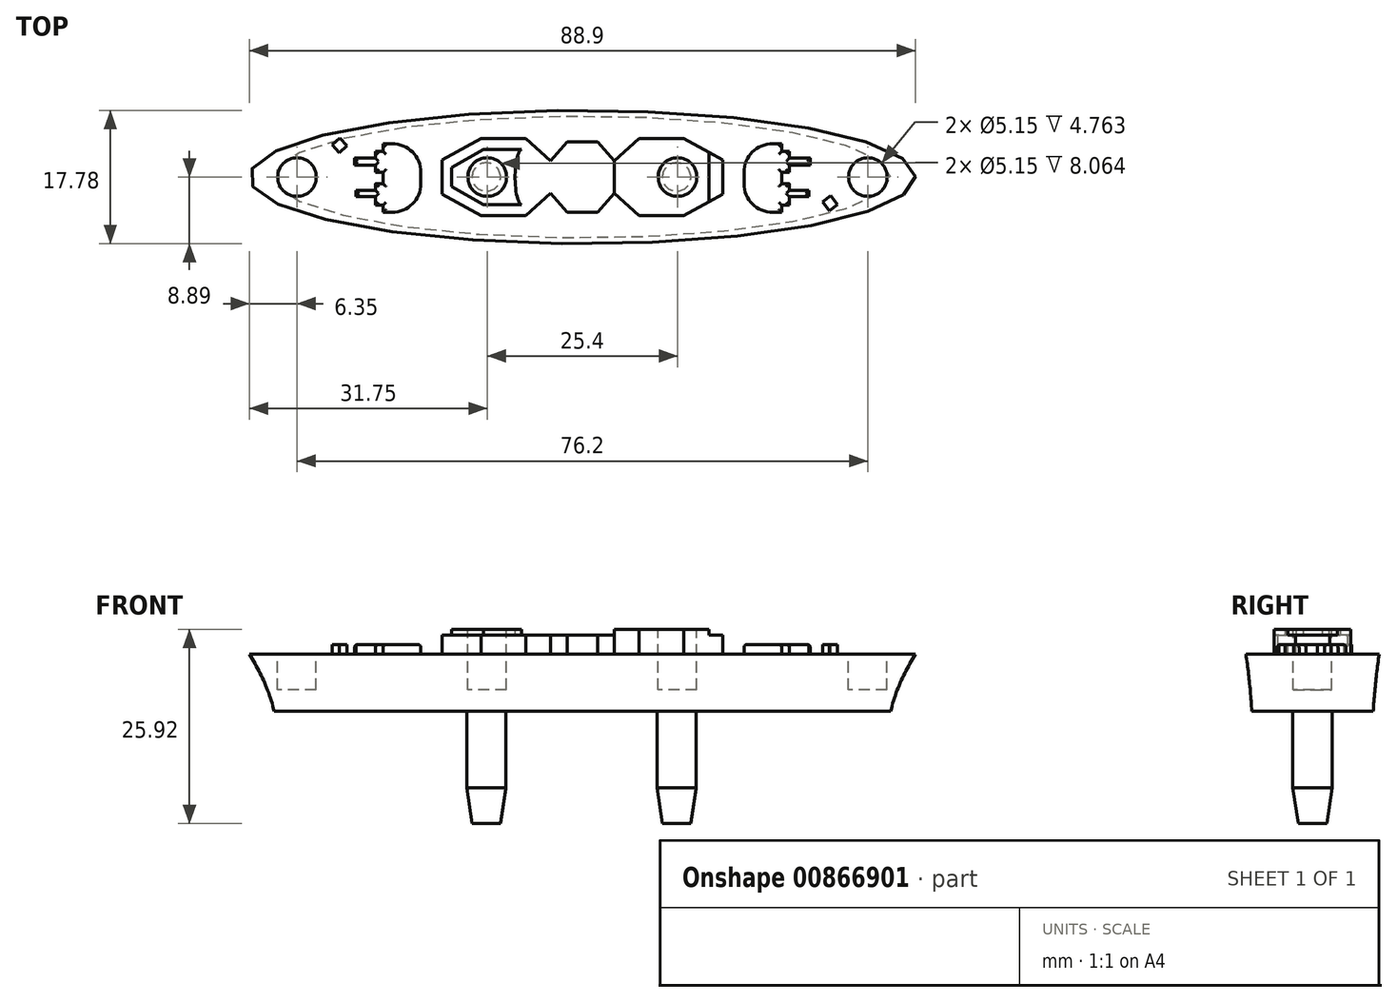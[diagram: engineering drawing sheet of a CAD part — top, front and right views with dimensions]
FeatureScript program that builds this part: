
annotation { "Feature Type Name" : "Feature", "Feature Type Description" : "" }
export const myFeature = defineFeature(function(context is Context, id is Id, definition is map)
    precondition{}
    {
        {
            var Q0;
            Q0=qCreatedBy(makeId("Top.planeOp"),FACE);
            var sketch = newSketch(context, id + "F0", { "sketchPlane" : qUnion([Q0])});
            skEllipse(sketch, "E0", {"center": v(0, 0) * mm, "majorRadius": 44.45 * mm, "minorRadius": 8.9 * mm, "majorAxis": v(1, 0)});
            skSolve(sketch);
        }
        {
            var Q0;
            Q0=qCreatedBy(makeId("Top.planeOp"),FACE);
            cPlane(context, id + "F1", {"entities" : qUnion([Q0]), "cplaneType" : CPlaneType.OFFSET, "offset" : 7.62 * mm, "oppositeDirection" : true, "width" : 152.4 * mm, "height" : 152.4 * mm});
        }
        {
            var Q0;
            Q0=qCreatedBy(id+"F1.planeOp",FACE);
            var sketch = newSketch(context, id + "F2", { "sketchPlane" : qUnion([Q0])});
            skEllipse(sketch, "E1", {"center": v(0, 0) * mm, "majorRadius": 41.16 * mm, "minorRadius": 8.1 * mm, "majorAxis": v(1, 0)});
            skSolve(sketch);
        }
        {
            var Q0;
            Q0=makeQuery(id+"F2.imprint","IMPRINT",FACE,{"disambiguationData":[TD([[makeQuery(id+"F2.imprint","IMPRINT",EDGE,{"derivedFrom":sQuery(id+"F2.wireOp",EDGE,"E1")}),1.0]])]});
            var Q1;
            Q1=makeQuery(id+"F0.imprint","IMPRINT",FACE,{"disambiguationData":[TD([[makeQuery(id+"F0.imprint","IMPRINT",EDGE,{"derivedFrom":sQuery(id+"F0.wireOp",EDGE,"E0")}),1.0]])]});
            loft(context, id + "F3", {"sheetProfilesArray" : [{ "sheetProfileEntities" : qUnion([Q0]) }, { "sheetProfileEntities" : qUnion([Q1]) }]});
        }
        {
            var Q0;
            Q0=qCreatedBy(id+"F1.planeOp",FACE);
            var sketch = newSketch(context, id + "F4", { "sketchPlane" : qUnion([Q0])});
            skLineSegment(sketch, "E2", {"start": v(-38.24, 0) * mm, "end": v(-12.84, 0) * mm, "construction": true});
            skLineSegment(sketch, "E3", {"start": v(-12.84, 0) * mm, "end": v(12.56, 0) * mm, "construction": true});
            skLineSegment(sketch, "E4", {"start": v(12.56, 0) * mm, "end": v(37.96, 0) * mm, "construction": true});
            skCircle(sketch, "E5", {"center": v(37.96, 0) * mm, "radius": 2.62 * mm});
            skCircle(sketch, "E6", {"center": v(12.56, 0) * mm, "radius": 2.62 * mm});
            skCircle(sketch, "E7", {"center": v(-12.84, 0) * mm, "radius": 2.62 * mm});
            skCircle(sketch, "E8", {"center": v(-38.24, 0) * mm, "radius": 2.62 * mm});
            skSolve(sketch);
        }
        {
            var Q0;
            Q0=makeQuery(id+"F4.imprint","IMPRINT",FACE,{"disambiguationData":[TD([[makeQuery(id+"F4.imprint","IMPRINT",EDGE,{"derivedFrom":sQuery(id+"F4.wireOp",EDGE,"E7")}),1.0]])]});
            var Q1;
            Q1=makeQuery(id+"F4.imprint","IMPRINT",FACE,{"disambiguationData":[TD([[makeQuery(id+"F4.imprint","IMPRINT",EDGE,{"derivedFrom":sQuery(id+"F4.wireOp",EDGE,"E6")}),1.0]])]});
            extrude(context, id + "F5", {"entities" : qUnion([Q0, Q1]), "operationType" : NewBodyOperationType.ADD, "oppositeDirection" : true, "depth" : 15 * mm, "offsetDistance" : 25.4 * mm});
        }
        {
            var Q0;
            Q0=makeQuery(id+"F3.opLoft","CAP_FACE",FACE,{"disambiguationData":[OSD([makeQuery(id+"F0.imprint","IMPRINT",FACE,{"disambiguationData":[TD([[makeQuery(id+"F0.imprint","IMPRINT",EDGE,{"derivedFrom":sQuery(id+"F0.wireOp",EDGE,"E0")}),1.0]])]})])],"isStart":true});
            var sketch = newSketch(context, id + "F6", { "sketchPlane" : qUnion([Q0])});
            skLineSegment(sketch, "E9", {"start": v(-38.1, 0) * mm, "end": v(-12.7, 0) * mm, "construction": true});
            skLineSegment(sketch, "E10", {"start": v(-12.7, 0) * mm, "end": v(12.7, 0) * mm, "construction": true});
            skLineSegment(sketch, "E11", {"start": v(12.7, 0) * mm, "end": v(38.1, 0) * mm, "construction": true});
            skCircle(sketch, "E12", {"center": v(38.1, 0) * mm, "radius": 2.58 * mm});
            skCircle(sketch, "E13", {"center": v(12.7, 0) * mm, "radius": 2.58 * mm});
            skCircle(sketch, "E14", {"center": v(-12.7, 0) * mm, "radius": 2.58 * mm});
            skCircle(sketch, "E15", {"center": v(-38.1, 0) * mm, "radius": 2.58 * mm});
            skSolve(sketch);
        }
        {
            var Q0;
            Q0=makeQuery(id+"F6.imprint","IMPRINT",FACE,{"disambiguationData":[TD([[makeQuery(id+"F6.imprint","IMPRINT",EDGE,{"derivedFrom":sQuery(id+"F6.wireOp",EDGE,"E15")}),1.0]])]});
            var Q1;
            Q1=makeQuery(id+"F6.imprint","IMPRINT",FACE,{"disambiguationData":[TD([[makeQuery(id+"F6.imprint","IMPRINT",EDGE,{"derivedFrom":sQuery(id+"F6.wireOp",EDGE,"E14")}),1.0]])]});
            var Q2;
            Q2=makeQuery(id+"F6.imprint","IMPRINT",FACE,{"disambiguationData":[TD([[makeQuery(id+"F6.imprint","IMPRINT",EDGE,{"derivedFrom":sQuery(id+"F6.wireOp",EDGE,"E13")}),1.0]])]});
            var Q3;
            Q3=makeQuery(id+"F6.imprint","IMPRINT",FACE,{"disambiguationData":[TD([[makeQuery(id+"F6.imprint","IMPRINT",EDGE,{"derivedFrom":sQuery(id+"F6.wireOp",EDGE,"E12")}),1.0]])]});
            extrude(context, id + "F7", {"entities" : qUnion([Q0, Q1, Q2, Q3]), "operationType" : NewBodyOperationType.REMOVE, "oppositeDirection" : true, "depth" : 4.76 * mm, "offsetDistance" : 25.4 * mm});
        }
        {
            var Q0;
            Q0=makeQuery(id+"F5.opExtrude","CAP_EDGE",EDGE,{"disambiguationData":[OSD([sQuery(id+"F4.wireOp",EDGE,"E7")])],"isStart":false});
            var Q1;
            Q1=makeQuery(id+"F5.opExtrude","CAP_EDGE",EDGE,{"disambiguationData":[OSD([sQuery(id+"F4.wireOp",EDGE,"E6")])],"isStart":false});
            chamfer(context, id + "F8", {"entities" : qUnion([Q0, Q1]), "chamferType" : ChamferType.TWO_OFFSETS, "width1" : 4.76 * mm, "oppositeDirection" : false, "width2" : 0.73 * mm, "tangentPropagation" : true});
        }
        {
            var Q0;
            Q0=makeQuery(id+"F3.opLoft","CAP_FACE",FACE,{"disambiguationData":[OSD([makeQuery(id+"F0.imprint","IMPRINT",FACE,{"disambiguationData":[TD([[makeQuery(id+"F0.imprint","IMPRINT",EDGE,{"derivedFrom":sQuery(id+"F0.wireOp",EDGE,"E0")}),1.0]])]})])],"isStart":true});
            var sketch = newSketch(context, id + "F9", { "sketchPlane" : qUnion([Q0])});
            skLineSegment(sketch, "E16", {"start": v(0, 11.72) * mm, "end": v(0, 15.23) * mm, "construction": true});
            skLineSegment(sketch, "E17", {"start": v(0, 4.68) * mm, "end": v(2.01, 4.68) * mm});
            skLineSegment(sketch, "E18", {"start": v(2.01, 4.68) * mm, "end": v(4.23, 2.18) * mm});
            skLineSegment(sketch, "E19", {"start": v(4.23, 2.18) * mm, "end": v(7.53, 5.12) * mm});
            skLineSegment(sketch, "E20", {"start": v(7.53, 5.12) * mm, "end": v(13.53, 5.12) * mm});
            skLineSegment(sketch, "E21", {"start": v(13.53, 5.12) * mm, "end": v(18.74, 2.3) * mm});
            skLineSegment(sketch, "E22", {"start": v(18.74, 2.3) * mm, "end": v(18.74, -2.3) * mm});
            skLineSegment(sketch, "E23", {"start": v(18.74, -2.3) * mm, "end": v(13.53, -5.12) * mm});
            skLineSegment(sketch, "E24", {"start": v(13.53, -5.12) * mm, "end": v(7.53, -5.12) * mm});
            skLineSegment(sketch, "E25", {"start": v(7.53, -5.12) * mm, "end": v(4.23, -2.18) * mm});
            skLineSegment(sketch, "E26", {"start": v(4.23, -2.18) * mm, "end": v(2.01, -4.68) * mm});
            skLineSegment(sketch, "E27", {"start": v(2.01, -4.68) * mm, "end": v(0, -4.68) * mm});
            skLineSegment(sketch, "E28.MirrorCS", {"start": v(-7.53, -5.12) * mm, "end": v(-4.23, -2.18) * mm});
            skLineSegment(sketch, "E29.MirrorCS", {"start": v(-4.23, -2.18) * mm, "end": v(-2.01, -4.68) * mm});
            skLineSegment(sketch, "E30.MirrorCS", {"start": v(-2.01, 4.68) * mm, "end": v(-4.23, 2.18) * mm});
            skLineSegment(sketch, "E31.MirrorCS", {"start": v(-4.23, 2.18) * mm, "end": v(-7.53, 5.12) * mm});
            skLineSegment(sketch, "E32.MirrorCS", {"start": v(-2.01, -4.68) * mm, "end": v(0, -4.68) * mm});
            skLineSegment(sketch, "E33.MirrorCS", {"start": v(0, 4.68) * mm, "end": v(-2.01, 4.68) * mm});
            skLineSegment(sketch, "E34.MirrorCS", {"start": v(-18.74, -2.3) * mm, "end": v(-13.53, -5.12) * mm});
            skLineSegment(sketch, "E35.MirrorCS", {"start": v(-13.53, -5.12) * mm, "end": v(-7.53, -5.12) * mm});
            skLineSegment(sketch, "E36.MirrorCS", {"start": v(-18.74, 2.3) * mm, "end": v(-18.74, -2.3) * mm});
            skLineSegment(sketch, "E37.MirrorCS", {"start": v(-13.53, 5.12) * mm, "end": v(-18.74, 2.3) * mm});
            skLineSegment(sketch, "E38.MirrorCS", {"start": v(-7.53, 5.12) * mm, "end": v(-13.53, 5.12) * mm});
            skLineSegment(sketch, "E39", {"start": v(12.7, 0) * mm, "end": v(-12.7, 0) * mm, "construction": true});
            skSolve(sketch);
        }
        {
            var Q0;
            Q0=makeQuery(id+"F9.imprint","IMPRINT",FACE,{"disambiguationData":[TD([[makeQuery(id+"F9.imprint","IMPRINT",EDGE,{"derivedFrom":sQuery(id+"F9.wireOp",EDGE,"E17")}),-1.0]])]});
            extrude(context, id + "F10", {"entities" : qUnion([Q0]), "operationType" : NewBodyOperationType.ADD, "depth" : 2.54 * mm, "offsetDistance" : 25.4 * mm});
        }
        {
            var Q0;
            Q0=makeQuery(id+"F10.opExtrude","CAP_FACE",FACE,{"disambiguationData":[OSD([sQuery(id+"F6.wireOp",EDGE,"E13"),sQuery(id+"F6.wireOp",EDGE,"E14"),sQuery(id+"F9.wireOp",EDGE,"E17"),sQuery(id+"F9.wireOp",EDGE,"E18"),sQuery(id+"F9.wireOp",EDGE,"E19"),sQuery(id+"F9.wireOp",EDGE,"E20"),sQuery(id+"F9.wireOp",EDGE,"E21"),sQuery(id+"F9.wireOp",EDGE,"E22"),sQuery(id+"F9.wireOp",EDGE,"E23"),sQuery(id+"F9.wireOp",EDGE,"E24"),sQuery(id+"F9.wireOp",EDGE,"E25"),sQuery(id+"F9.wireOp",EDGE,"E26"),sQuery(id+"F9.wireOp",EDGE,"E27"),sQuery(id+"F9.wireOp",EDGE,"E28.MirrorCS"),sQuery(id+"F9.wireOp",EDGE,"E29.MirrorCS"),sQuery(id+"F9.wireOp",EDGE,"E30.MirrorCS"),sQuery(id+"F9.wireOp",EDGE,"E31.MirrorCS"),sQuery(id+"F9.wireOp",EDGE,"E32.MirrorCS"),sQuery(id+"F9.wireOp",EDGE,"E33.MirrorCS"),sQuery(id+"F9.wireOp",EDGE,"E34.MirrorCS"),sQuery(id+"F9.wireOp",EDGE,"E35.MirrorCS"),sQuery(id+"F9.wireOp",EDGE,"E36.MirrorCS"),sQuery(id+"F9.wireOp",EDGE,"E37.MirrorCS"),sQuery(id+"F9.wireOp",EDGE,"E38.MirrorCS")])],"isStart":false});
            var sketch = newSketch(context, id + "F11", { "sketchPlane" : qUnion([Q0])});
            skLineSegment(sketch, "E40", {"start": v(-8.16, 3.7) * mm, "end": v(-13.2, 3.7) * mm});
            skLineSegment(sketch, "E41", {"start": v(-13.2, -3.7) * mm, "end": v(-8.16, -3.7) * mm});
            skPoint(sketch, "E42", {"position": v(-4.23, 1.21) * mm});
            skPoint(sketch, "E43", {"position": v(0, 3.64) * mm});
            skPoint(sketch, "E44", {"position": v(2.47, 0) * mm});
            skPoint(sketch, "E45", {"position": v(0, -3.64) * mm});
            skPoint(sketch, "E46", {"position": v(-4.23, -1.21) * mm});
            skFitSpline(sketch, "E47", {"points": [v(-8.16, 3.7) * mm, v(-4.23, 1.21) * mm, v(0, 3.64) * mm, v(2.47, 0) * mm, v(0, -3.64) * mm, v(-4.23, -1.21) * mm, v(-8.16, -3.7) * mm, v(-8.16, 3.7) * mm]});
            skLineSegment(sketch, "E48", {"start": v(7.53, 5.12) * mm, "end": v(4.23, 2.18) * mm});
            skLineSegment(sketch, "E49", {"start": v(4.23, -2.18) * mm, "end": v(7.53, -5.12) * mm});
            skLineSegment(sketch, "E50", {"start": v(7.53, -5.12) * mm, "end": v(13.53, -5.12) * mm});
            skLineSegment(sketch, "E51", {"start": v(13.53, 5.12) * mm, "end": v(7.53, 5.12) * mm});
            skLineSegment(sketch, "E52", {"start": v(-12.7, 0) * mm, "end": v(12.7, 0) * mm, "construction": true});
            skPoint(sketch, "E53", {"position": v(-17.44, 1.26) * mm});
            skPoint(sketch, "E54", {"position": v(-17.44, -1.26) * mm});
            skLineSegment(sketch, "E55", {"start": v(-13.2, 3.7) * mm, "end": v(-17.44, 1.26) * mm});
            skLineSegment(sketch, "E56", {"start": v(-17.44, 1.26) * mm, "end": v(-17.44, -1.26) * mm});
            skLineSegment(sketch, "E57", {"start": v(-17.44, -1.26) * mm, "end": v(-13.2, -3.7) * mm});
            skPoint(sketch, "E58", {"position": v(16.9, 3.29) * mm});
            skPoint(sketch, "E59", {"position": v(16.9, -3.29) * mm});
            skLineSegment(sketch, "E60", {"start": v(13.53, 5.12) * mm, "end": v(16.9, 3.29) * mm});
            skLineSegment(sketch, "E61", {"start": v(16.9, 3.29) * mm, "end": v(16.9, -3.29) * mm});
            skLineSegment(sketch, "E62", {"start": v(16.9, -3.29) * mm, "end": v(13.53, -5.12) * mm});
            skLineSegment(sketch, "E63", {"start": v(4.23, 2.18) * mm, "end": v(4.23, -2.18) * mm});
            skSolve(sketch);
        }
        {
            var Q0;
            Q0=makeQuery(id+"F11.imprint","IMPRINT",FACE,{"disambiguationData":[TD([[makeQuery(id+"F11.imprint","IMPRINT",EDGE,{"derivedFrom":sQuery(id+"F11.wireOp",EDGE,"E40")}),1.0]])]});
            var Q1;
            Q1=makeQuery(id+"F11.imprint","IMPRINT",FACE,{"disambiguationData":[TD([[makeQuery(id+"F11.imprint","IMPRINT",EDGE,{"derivedFrom":sQuery(id+"F11.wireOp",EDGE,"E48")}),-1.0]])]});
            extrude(context, id + "F12", {"entities" : qUnion([Q0, Q1]), "operationType" : NewBodyOperationType.ADD, "depth" : 0.76 * mm, "offsetDistance" : 25.4 * mm});
        }
        {
            var Q0;
            Q0=makeQuery(id+"F3.opLoft","CAP_FACE",FACE,{"disambiguationData":[OSD([makeQuery(id+"F0.imprint","IMPRINT",FACE,{"disambiguationData":[TD([[makeQuery(id+"F0.imprint","IMPRINT",EDGE,{"derivedFrom":sQuery(id+"F0.wireOp",EDGE,"E0")}),1.0]])]})])],"isStart":true});
            var sketch = newSketch(context, id + "F13", { "sketchPlane" : qUnion([Q0])});
            skLineSegment(sketch, "E64", {"start": v(0, -10.91) * mm, "end": v(0, -13.7) * mm, "construction": true});
            skLineSegment(sketch, "E65.bottom", {"start": v(25.38, 4.45) * mm, "end": v(26.6, 4.45) * mm});
            skLineSegment(sketch, "E65.top", {"start": v(25.38, -4.7) * mm, "end": v(26.6, -4.7) * mm});
            skLineSegment(sketch, "E65.left", {"start": v(21.57, 0.64) * mm, "end": v(21.57, -0.9) * mm});
            skLineSegment(sketch, "E65.right", {"start": v(26.6, 4.45) * mm, "end": v(26.6, 3.41) * mm});
            skPoint(sketch, "E66.visualSharp", {"position": v(21.57, 4.45) * mm});
            skArc(sketch, "E66.filletArc", {"start": v(25.38, 4.45) * mm, "mid": v(22.68, 3.33) * mm, "end": v(21.57, 0.64) * mm});
            skPoint(sketch, "E67.visualSharp", {"position": v(21.57, -4.7) * mm});
            skArc(sketch, "E67.filletArc", {"start": v(21.57, -0.9) * mm, "mid": v(22.68, -3.6) * mm, "end": v(25.38, -4.7) * mm});
            skLineSegment(sketch, "E68.bottom", {"start": v(26.6, 3.41) * mm, "end": v(27.6, 3.41) * mm});
            skLineSegment(sketch, "E68.top", {"start": v(26.6, 0.62) * mm, "end": v(27.6, 0.62) * mm});
            skLineSegment(sketch, "E68.right", {"start": v(27.6, 3.41) * mm, "end": v(27.6, 2.5) * mm});
            skLineSegment(sketch, "E69.bottom", {"start": v(26.6, -0.89) * mm, "end": v(27.6, -0.89) * mm});
            skLineSegment(sketch, "E69.top", {"start": v(26.6, -3.75) * mm, "end": v(27.6, -3.75) * mm});
            skLineSegment(sketch, "E69.right", {"start": v(27.6, -0.89) * mm, "end": v(27.6, -1.8) * mm});
            skLineSegment(sketch, "E70.bottom", {"start": v(27.6, 2.5) * mm, "end": v(30.4, 2.5) * mm});
            skLineSegment(sketch, "E70.top", {"start": v(27.6, 1.6) * mm, "end": v(30.4, 1.6) * mm});
            skLineSegment(sketch, "E70.right", {"start": v(30.4, 2.5) * mm, "end": v(30.4, 1.6) * mm});
            skLineSegment(sketch, "E71.bottom", {"start": v(27.6, -1.8) * mm, "end": v(30.25, -1.8) * mm});
            skLineSegment(sketch, "E71.top", {"start": v(27.6, -2.62) * mm, "end": v(30.25, -2.62) * mm});
            skLineSegment(sketch, "E71.right", {"start": v(30.25, -1.8) * mm, "end": v(30.25, -2.62) * mm});
            skLineSegment(sketch, "E72.trimOffspring", {"start": v(27.6, 1.6) * mm, "end": v(27.6, 0.62) * mm});
            skLineSegment(sketch, "E73.trimOffspring", {"start": v(27.6, -2.62) * mm, "end": v(27.6, -3.75) * mm});
            skLineSegment(sketch, "E74.trimOffspring", {"start": v(26.6, -3.75) * mm, "end": v(26.6, -4.7) * mm});
            skLineSegment(sketch, "E75.trimOffspring", {"start": v(26.6, 0.62) * mm, "end": v(26.6, -0.89) * mm});
            skLineSegment(sketch, "E76.MirrorCS", {"start": v(-27.6, -0.89) * mm, "end": v(-27.6, -1.8) * mm});
            skLineSegment(sketch, "E77.MirrorCS", {"start": v(-26.6, -0.89) * mm, "end": v(-27.6, -0.89) * mm});
            skLineSegment(sketch, "E78.MirrorCS", {"start": v(-26.6, 0.62) * mm, "end": v(-27.6, 0.62) * mm});
            skLineSegment(sketch, "E79.MirrorCS", {"start": v(-27.6, 1.6) * mm, "end": v(-27.6, 0.62) * mm});
            skLineSegment(sketch, "E80.MirrorCS", {"start": v(-26.6, 0.62) * mm, "end": v(-26.6, -0.89) * mm});
            skLineSegment(sketch, "E81.MirrorCS", {"start": v(-27.6, -2.62) * mm, "end": v(-27.6, -3.75) * mm});
            skLineSegment(sketch, "E82.MirrorCS", {"start": v(-30.25, -1.8) * mm, "end": v(-30.25, -2.62) * mm});
            skLineSegment(sketch, "E83.MirrorCS", {"start": v(-26.6, -3.75) * mm, "end": v(-26.6, -4.7) * mm});
            skLineSegment(sketch, "E84.MirrorCS", {"start": v(-26.6, 3.41) * mm, "end": v(-27.6, 3.41) * mm});
            skLineSegment(sketch, "E85.MirrorCS", {"start": v(-21.57, 0.64) * mm, "end": v(-21.57, -0.9) * mm});
            skLineSegment(sketch, "E86.MirrorCS", {"start": v(-25.38, 4.45) * mm, "end": v(-26.6, 4.45) * mm});
            skLineSegment(sketch, "E87.MirrorCS", {"start": v(-26.6, -3.75) * mm, "end": v(-27.6, -3.75) * mm});
            skLineSegment(sketch, "E88.MirrorCS", {"start": v(-27.6, 3.41) * mm, "end": v(-27.6, 2.5) * mm});
            skLineSegment(sketch, "E89.MirrorCS", {"start": v(-30.4, 2.5) * mm, "end": v(-30.4, 1.6) * mm});
            skLineSegment(sketch, "E90.MirrorCS", {"start": v(-27.6, -2.62) * mm, "end": v(-30.25, -2.62) * mm});
            skLineSegment(sketch, "E91.MirrorCS", {"start": v(-27.6, -1.8) * mm, "end": v(-30.25, -1.8) * mm});
            skLineSegment(sketch, "E92.MirrorCS", {"start": v(-25.38, -4.7) * mm, "end": v(-26.6, -4.7) * mm});
            skLineSegment(sketch, "E93.MirrorCS", {"start": v(-26.6, 4.45) * mm, "end": v(-26.6, 3.41) * mm});
            skPoint(sketch, "E94.MirrorP", {"position": v(-21.57, -4.7) * mm});
            skArc(sketch, "E95.MirrorCS", {"start": v(-25.38, 4.45) * mm, "mid": v(-22.68, 3.33) * mm, "end": v(-21.57, 0.64) * mm});
            skArc(sketch, "E96.MirrorCS", {"start": v(-21.57, -0.9) * mm, "mid": v(-22.68, -3.6) * mm, "end": v(-25.38, -4.7) * mm});
            skPoint(sketch, "E97.MirrorP", {"position": v(-21.57, 4.45) * mm});
            skLineSegment(sketch, "E98.MirrorCS", {"start": v(-27.6, 1.6) * mm, "end": v(-30.4, 1.6) * mm});
            skLineSegment(sketch, "E99.MirrorCS", {"start": v(-27.6, 2.5) * mm, "end": v(-30.4, 2.5) * mm});
            skLineSegment(sketch, "E100", {"start": v(-32.4, 5.21) * mm, "end": v(-33.39, 4.3) * mm});
            skLineSegment(sketch, "E101", {"start": v(-33.39, 4.3) * mm, "end": v(-32.43, 3.25) * mm});
            skLineSegment(sketch, "E102", {"start": v(-32.43, 3.25) * mm, "end": v(-31.43, 4.16) * mm});
            skLineSegment(sketch, "E103", {"start": v(-31.43, 4.16) * mm, "end": v(-32.4, 5.21) * mm});
            skLineSegment(sketch, "E104", {"start": v(33.12, -2.5) * mm, "end": v(32.06, -3.33) * mm});
            skLineSegment(sketch, "E105", {"start": v(32.06, -3.33) * mm, "end": v(32.99, -4.52) * mm});
            skLineSegment(sketch, "E106", {"start": v(32.99, -4.52) * mm, "end": v(34.05, -3.69) * mm});
            skLineSegment(sketch, "E107", {"start": v(34.05, -3.69) * mm, "end": v(33.12, -2.5) * mm});
            skSolve(sketch);
        }
        {
            var Q0;
            Q0=makeQuery(id+"F13.imprint","IMPRINT",FACE,{"disambiguationData":[TD([[makeQuery(id+"F13.imprint","IMPRINT",EDGE,{"derivedFrom":sQuery(id+"F13.wireOp",EDGE,"E76.MirrorCS")}),1.0]])]});
            var Q1;
            Q1=makeQuery(id+"F13.imprint","IMPRINT",FACE,{"disambiguationData":[TD([[makeQuery(id+"F13.imprint","IMPRINT",EDGE,{"derivedFrom":sQuery(id+"F13.wireOp",EDGE,"E65.bottom")}),-1.0]])]});
            var Q2;
            Q2=makeQuery(id+"F13.imprint","IMPRINT",FACE,{"disambiguationData":[TD([[makeQuery(id+"F13.imprint","IMPRINT",EDGE,{"derivedFrom":sQuery(id+"F13.wireOp",EDGE,"E100")}),1.0]])]});
            var Q3;
            Q3=makeQuery(id+"F13.imprint","IMPRINT",FACE,{"disambiguationData":[TD([[makeQuery(id+"F13.imprint","IMPRINT",EDGE,{"derivedFrom":sQuery(id+"F13.wireOp",EDGE,"E104")}),1.0]])]});
            extrude(context, id + "F14", {"entities" : qUnion([Q0, Q1, Q2, Q3]), "operationType" : NewBodyOperationType.ADD, "depth" : 1.27 * mm, "offsetDistance" : 25.4 * mm});
        }
        {
            var Q0;
            Q0=makeQuery(id+"F14.opExtrude","CAP_FACE",FACE,{"disambiguationData":[OSD([sQuery(id+"F13.wireOp",EDGE,"E76.MirrorCS"),sQuery(id+"F13.wireOp",EDGE,"E77.MirrorCS"),sQuery(id+"F13.wireOp",EDGE,"E78.MirrorCS"),sQuery(id+"F13.wireOp",EDGE,"E79.MirrorCS"),sQuery(id+"F13.wireOp",EDGE,"E80.MirrorCS"),sQuery(id+"F13.wireOp",EDGE,"E81.MirrorCS"),sQuery(id+"F13.wireOp",EDGE,"E82.MirrorCS"),sQuery(id+"F13.wireOp",EDGE,"E83.MirrorCS"),sQuery(id+"F13.wireOp",EDGE,"E84.MirrorCS"),sQuery(id+"F13.wireOp",EDGE,"E85.MirrorCS"),sQuery(id+"F13.wireOp",EDGE,"E86.MirrorCS"),sQuery(id+"F13.wireOp",EDGE,"E87.MirrorCS"),sQuery(id+"F13.wireOp",EDGE,"E88.MirrorCS"),sQuery(id+"F13.wireOp",EDGE,"E89.MirrorCS"),sQuery(id+"F13.wireOp",EDGE,"E90.MirrorCS"),sQuery(id+"F13.wireOp",EDGE,"E91.MirrorCS"),sQuery(id+"F13.wireOp",EDGE,"E92.MirrorCS"),sQuery(id+"F13.wireOp",EDGE,"E93.MirrorCS"),sQuery(id+"F13.wireOp",EDGE,"E95.MirrorCS"),sQuery(id+"F13.wireOp",EDGE,"E96.MirrorCS"),sQuery(id+"F13.wireOp",EDGE,"E98.MirrorCS"),sQuery(id+"F13.wireOp",EDGE,"E99.MirrorCS")])],"isStart":false});
            var Q1;
            Q1=makeQuery(id+"F14.opExtrude","CAP_FACE",FACE,{"disambiguationData":[OSD([sQuery(id+"F13.wireOp",EDGE,"E65.bottom"),sQuery(id+"F13.wireOp",EDGE,"E65.top"),sQuery(id+"F13.wireOp",EDGE,"E65.left"),sQuery(id+"F13.wireOp",EDGE,"E65.right"),sQuery(id+"F13.wireOp",EDGE,"E66.filletArc"),sQuery(id+"F13.wireOp",EDGE,"E67.filletArc"),sQuery(id+"F13.wireOp",EDGE,"E68.bottom"),sQuery(id+"F13.wireOp",EDGE,"E68.top"),sQuery(id+"F13.wireOp",EDGE,"E68.right"),sQuery(id+"F13.wireOp",EDGE,"E69.bottom"),sQuery(id+"F13.wireOp",EDGE,"E69.top"),sQuery(id+"F13.wireOp",EDGE,"E69.right"),sQuery(id+"F13.wireOp",EDGE,"E70.bottom"),sQuery(id+"F13.wireOp",EDGE,"E70.top"),sQuery(id+"F13.wireOp",EDGE,"E70.right"),sQuery(id+"F13.wireOp",EDGE,"E71.bottom"),sQuery(id+"F13.wireOp",EDGE,"E71.top"),sQuery(id+"F13.wireOp",EDGE,"E71.right"),sQuery(id+"F13.wireOp",EDGE,"E72.trimOffspring"),sQuery(id+"F13.wireOp",EDGE,"E73.trimOffspring"),sQuery(id+"F13.wireOp",EDGE,"E74.trimOffspring"),sQuery(id+"F13.wireOp",EDGE,"E75.trimOffspring")])],"isStart":false});
            fillet(context, id + "F15", {"entities" : qUnion([Q0, Q1]), "radius" : 0.38 * mm, "tangentPropagation" : true, "allowEdgeOverflow" : false});
        }
    });
